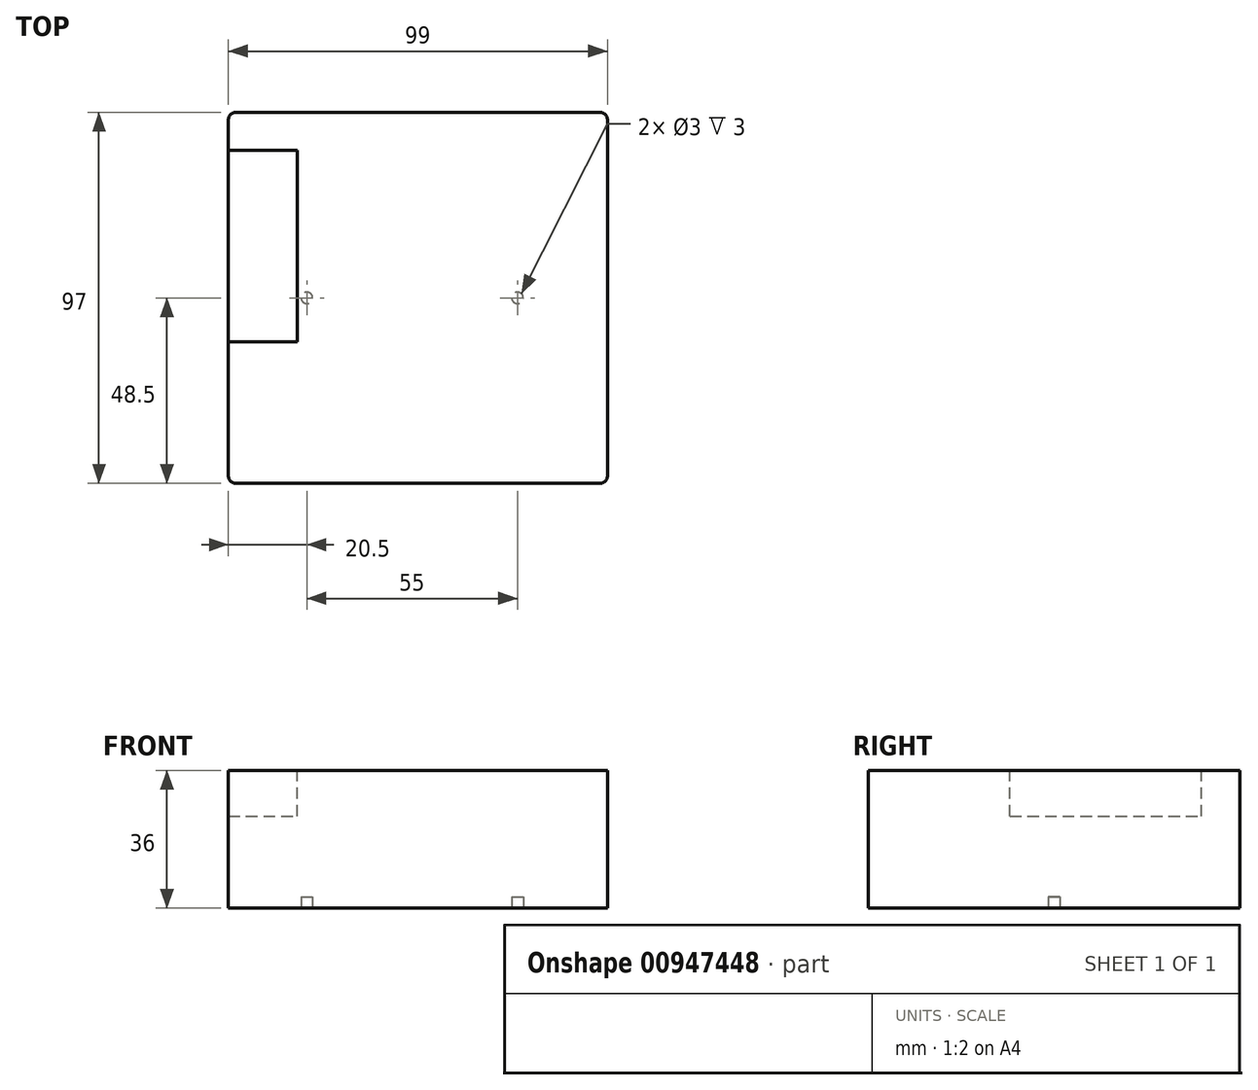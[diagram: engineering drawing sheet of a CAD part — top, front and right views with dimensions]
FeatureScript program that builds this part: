
annotation { "Feature Type Name" : "Feature", "Feature Type Description" : "" }
export const myFeature = defineFeature(function(context is Context, id is Id, definition is map)
    precondition{}
    {
        {
            var Q0;
            Q0=qCreatedBy(makeId("Top.planeOp"),FACE);
            var sketch = newSketch(context, id + "F0", { "sketchPlane" : qUnion([Q0])});
            skLineSegment(sketch, "E0.bottom", {"start": v(49.5, -48.5) * mm, "end": v(-49.5, -48.5) * mm});
            skLineSegment(sketch, "E0.top", {"start": v(49.5, 48.5) * mm, "end": v(-49.5, 48.5) * mm});
            skLineSegment(sketch, "E0.left", {"start": v(49.5, -48.5) * mm, "end": v(49.5, 48.5) * mm});
            skLineSegment(sketch, "E0.right", {"start": v(-49.5, -48.5) * mm, "end": v(-49.5, 48.5) * mm});
            skPoint(sketch, "E0.middle", {"position": v(0, 0) * mm});
            skSolve(sketch);
        }
        {
            var Q0;
            Q0=makeQuery(id+"F0.imprint","IMPRINT",FACE,{"disambiguationData":[TD([[makeQuery(id+"F0.imprint","IMPRINT",EDGE,{"derivedFrom":sQuery(id+"F0.wireOp",EDGE,"E0.bottom")}),-1.0]])]});
            extrude(context, id + "F1", {"entities" : qUnion([Q0]), "depth" : 36 * mm, "offsetDistance" : 25 * mm});
        }
        {
            var Q0;
            Q0=makeQuery(id+"F1.opExtrude","CAP_FACE",FACE,{"disambiguationData":[OSD([sQuery(id+"F0.wireOp",EDGE,"E0.bottom"),sQuery(id+"F0.wireOp",EDGE,"E0.top"),sQuery(id+"F0.wireOp",EDGE,"E0.left"),sQuery(id+"F0.wireOp",EDGE,"E0.right")])],"isStart":true});
            var sketch = newSketch(context, id + "F2", { "sketchPlane" : qUnion([Q0])});
            skCircle(sketch, "E1", {"center": v(-29, 0) * mm, "radius": 1.5 * mm});
            skCircle(sketch, "E2", {"center": v(26, 0) * mm, "radius": 1.5 * mm});
            skSolve(sketch);
        }
        {
            var Q0;
            Q0=makeQuery(id+"F2.imprint","IMPRINT",FACE,{"disambiguationData":[TD([[makeQuery(id+"F2.imprint","IMPRINT",EDGE,{"derivedFrom":sQuery(id+"F2.wireOp",EDGE,"E1")}),1.0]])]});
            var Q1;
            Q1=makeQuery(id+"F2.imprint","IMPRINT",FACE,{"disambiguationData":[TD([[makeQuery(id+"F2.imprint","IMPRINT",EDGE,{"derivedFrom":sQuery(id+"F2.wireOp",EDGE,"E2")}),1.0]])]});
            extrude(context, id + "F3", {"entities" : qUnion([Q0, Q1]), "operationType" : NewBodyOperationType.REMOVE, "oppositeDirection" : true, "depth" : 3 * mm, "offsetDistance" : 25 * mm});
        }
        {
            var Q0;
            Q0=makeQuery(id+"F1.opExtrude","CAP_FACE",FACE,{"disambiguationData":[OSD([sQuery(id+"F0.wireOp",EDGE,"E0.bottom"),sQuery(id+"F0.wireOp",EDGE,"E0.top"),sQuery(id+"F0.wireOp",EDGE,"E0.left"),sQuery(id+"F0.wireOp",EDGE,"E0.right")])],"isStart":false});
            var sketch = newSketch(context, id + "F4", { "sketchPlane" : qUnion([Q0])});
            skLineSegment(sketch, "E3.bottom", {"start": v(-49.5, 38.5) * mm, "end": v(-31.5, 38.5) * mm});
            skLineSegment(sketch, "E3.top", {"start": v(-49.5, -11.5) * mm, "end": v(-31.5, -11.5) * mm});
            skLineSegment(sketch, "E3.left", {"start": v(-49.5, 38.5) * mm, "end": v(-49.5, -11.5) * mm});
            skLineSegment(sketch, "E3.right", {"start": v(-31.5, 38.5) * mm, "end": v(-31.5, -11.5) * mm});
            skSolve(sketch);
        }
        {
            var Q0;
            Q0=makeQuery(id+"F4.imprint","IMPRINT",FACE,{"disambiguationData":[TD([[makeQuery(id+"F4.imprint","IMPRINT",EDGE,{"derivedFrom":sQuery(id+"F4.wireOp",EDGE,"E3.bottom")}),-1.0]])]});
            extrude(context, id + "F5", {"entities" : qUnion([Q0]), "operationType" : NewBodyOperationType.REMOVE, "oppositeDirection" : true, "depth" : 12 * mm, "offsetDistance" : 25 * mm});
        }
        {
            var Q0;
            Q0=makeQuery(id+"F1.opExtrude","SWEPT_EDGE",EDGE,{"disambiguationData":[OSD([sQuery(id+"F0.wireOp",EDGE,"E0.bottom"),sQuery(id+"F0.wireOp",EDGE,"E0.right")])]});
            var Q1;
            Q1=makeQuery(id+"F1.opExtrude","SWEPT_EDGE",EDGE,{"disambiguationData":[OSD([sQuery(id+"F0.wireOp",EDGE,"E0.bottom"),sQuery(id+"F0.wireOp",EDGE,"E0.left")])]});
            var Q2;
            Q2=makeQuery(id+"F1.opExtrude","SWEPT_EDGE",EDGE,{"disambiguationData":[OSD([sQuery(id+"F0.wireOp",EDGE,"E0.top"),sQuery(id+"F0.wireOp",EDGE,"E0.left")])]});
            var Q3;
            Q3=makeQuery(id+"F1.opExtrude","SWEPT_EDGE",EDGE,{"disambiguationData":[OSD([sQuery(id+"F0.wireOp",EDGE,"E0.top"),sQuery(id+"F0.wireOp",EDGE,"E0.right")])]});
            fillet(context, id + "F6", {"entities" : qUnion([Q0, Q1, Q2, Q3]), "radius" : 2 * mm, "tangentPropagation" : true, "allowEdgeOverflow" : false});
        }
    });
